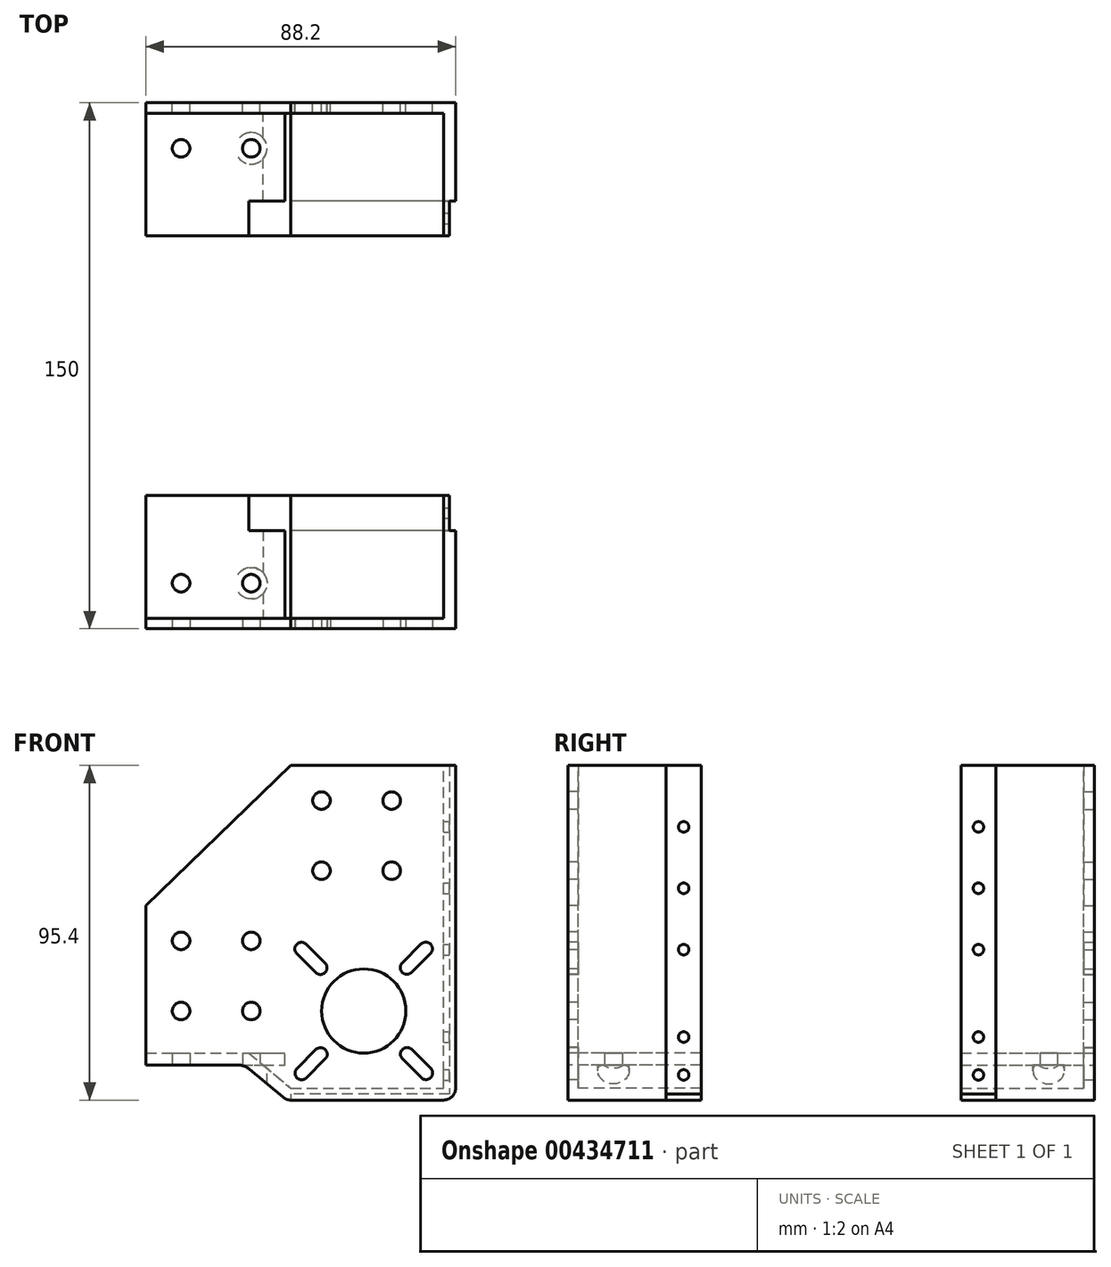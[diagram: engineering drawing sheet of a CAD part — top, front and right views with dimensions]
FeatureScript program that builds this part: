
annotation { "Feature Type Name" : "Feature", "Feature Type Description" : "" }
export const myFeature = defineFeature(function(context is Context, id is Id, definition is map)
    precondition{}
    {
        {
            assignVariable(context, id + "F0", {"name" : "Thickness", "anyValue" : 3});
        }
        {
            var Q0;
            Q0=qCreatedBy(makeId("Front.planeOp"),FACE);
            cPlane(context, id + "F1", {"entities" : qUnion([Q0]), "cplaneType" : CPlaneType.OFFSET, "offset" : 75 * mm, "width" : 150 * mm, "height" : 150 * mm});
        }
        {
            var Q0;
            Q0=qCreatedBy(id+"F1.planeOp",FACE);
            var sketch = newSketch(context, id + "F2", { "sketchPlane" : qUnion([Q0])});
            skLineSegment(sketch, "E0.bottom", {"start": v(-20, 20) * mm, "end": v(20, 20) * mm, "construction": true});
            skLineSegment(sketch, "E0.top", {"start": v(-20, -20) * mm, "end": v(20, -20) * mm, "construction": true});
            skLineSegment(sketch, "E0.left", {"start": v(-20, 20) * mm, "end": v(-20, -20) * mm, "construction": true});
            skLineSegment(sketch, "E0.right", {"start": v(20, 20) * mm, "end": v(20, -20) * mm, "construction": true});
            skLineSegment(sketch, "E1", {"start": v(0, 77.82) * mm, "end": v(0, -77.82) * mm, "construction": true});
            skLineSegment(sketch, "E2", {"start": v(-61.46, 0) * mm, "end": v(61.46, 0) * mm, "construction": true});
            skLineSegment(sketch, "E3", {"start": v(20, 20) * mm, "end": v(-20, -20) * mm, "construction": true});
            skLineSegment(sketch, "E4", {"start": v(-20, 20) * mm, "end": v(20, -20) * mm, "construction": true});
            skPoint(sketch, "E5", {"position": v(-15, 15) * mm});
            skPoint(sketch, "E6", {"position": v(-15, -15) * mm});
            skPoint(sketch, "E7", {"position": v(15, 15) * mm});
            skPoint(sketch, "E8", {"position": v(15, -15) * mm});
            skCircle(sketch, "E9", {"center": v(-15, 15) * mm, "radius": 1.9 * mm, "construction": true});
            skLineSegment(sketch, "E10", {"start": v(-17.69, 17.69) * mm, "end": v(-21.46, 13.92) * mm, "construction": true});
            skLineSegment(sketch, "E11", {"start": v(-17.69, 17.69) * mm, "end": v(-15.39, 19.99) * mm, "construction": true});
            skLineSegment(sketch, "E12", {"start": v(-12.31, 12.31) * mm, "end": v(-14.6, 10.03) * mm, "construction": true});
            skLineSegment(sketch, "E13", {"start": v(-12.31, 12.31) * mm, "end": v(-10.18, 14.45) * mm, "construction": true});
            skLineSegment(sketch, "E14", {"start": v(-19.03, 16.34) * mm, "end": v(-13.66, 10.97) * mm});
            skLineSegment(sketch, "E15", {"start": v(-16.34, 19.03) * mm, "end": v(-10.97, 13.66) * mm});
            skArc(sketch, "E16", {"start": v(-16.34, 19.03) * mm, "mid": v(-19.03, 19.03) * mm, "end": v(-19.03, 16.34) * mm});
            skArc(sketch, "E17", {"start": v(-19.03, 16.34) * mm, "mid": v(-16.34, 16.34) * mm, "end": v(-16.34, 19.03) * mm, "construction": true});
            skArc(sketch, "E18", {"start": v(-10.97, 13.66) * mm, "mid": v(-13.66, 13.66) * mm, "end": v(-13.66, 10.97) * mm, "construction": true});
            skArc(sketch, "E19", {"start": v(-13.66, 10.97) * mm, "mid": v(-10.97, 10.97) * mm, "end": v(-10.97, 13.66) * mm});
            skArc(sketch, "E20.1.0", {"start": v(-10.91, -13.7) * mm, "mid": v(-10.91, -11) * mm, "end": v(-13.6, -11) * mm});
            skLineSegment(sketch, "E20.1.1", {"start": v(-16.29, -19.07) * mm, "end": v(-10.91, -13.7) * mm});
            skArc(sketch, "E20.1.2", {"start": v(-18.98, -16.38) * mm, "mid": v(-18.98, -19.07) * mm, "end": v(-16.29, -19.07) * mm});
            skLineSegment(sketch, "E20.1.3", {"start": v(-18.98, -16.38) * mm, "end": v(-13.6, -11) * mm});
            skArc(sketch, "E20.2.0", {"start": v(13.75, -10.95) * mm, "mid": v(11.06, -10.95) * mm, "end": v(11.06, -13.64) * mm});
            skLineSegment(sketch, "E20.2.1", {"start": v(19.12, -16.33) * mm, "end": v(13.75, -10.95) * mm});
            skArc(sketch, "E20.2.2", {"start": v(16.44, -19.01) * mm, "mid": v(19.12, -19.01) * mm, "end": v(19.12, -16.33) * mm});
            skLineSegment(sketch, "E20.2.3", {"start": v(16.44, -19.01) * mm, "end": v(11.06, -13.64) * mm});
            skArc(sketch, "E20.3.0", {"start": v(11, 13.71) * mm, "mid": v(11, 11.02) * mm, "end": v(13.7, 11.02) * mm});
            skLineSegment(sketch, "E20.3.1", {"start": v(16.38, 19.09) * mm, "end": v(11, 13.71) * mm});
            skArc(sketch, "E20.3.2", {"start": v(19.07, 16.4) * mm, "mid": v(19.07, 19.09) * mm, "end": v(16.38, 19.09) * mm});
            skLineSegment(sketch, "E20.3.3", {"start": v(19.07, 16.4) * mm, "end": v(13.7, 11.02) * mm});
            skPoint(sketch, "E20.center", {"position": v(0.05, 0) * mm});
            skCircle(sketch, "E21", {"center": v(0.05, 0) * mm, "radius": 12 * mm});
            skSolve(sketch);
        }
        {
            var Q0;
            Q0=qCreatedBy(id+"F1.planeOp",FACE);
            var sketch = newSketch(context, id + "F3", { "sketchPlane" : qUnion([Q0])});
            skCircle(sketch, "E22.0", {"center": v(0.05, 0) * mm, "radius": 12 * mm});
            skArc(sketch, "E22.1", {"start": v(-13.66, 10.97) * mm, "mid": v(-10.97, 10.97) * mm, "end": v(-10.97, 13.66) * mm});
            skLineSegment(sketch, "E22.2", {"start": v(-16.34, 19.03) * mm, "end": v(-10.97, 13.66) * mm});
            skArc(sketch, "E22.3", {"start": v(-16.34, 19.03) * mm, "mid": v(-19.03, 19.03) * mm, "end": v(-19.03, 16.34) * mm});
            skLineSegment(sketch, "E22.4", {"start": v(-19.03, 16.34) * mm, "end": v(-13.66, 10.97) * mm});
            skLineSegment(sketch, "E22.5", {"start": v(16.38, 19.09) * mm, "end": v(11, 13.71) * mm});
            skArc(sketch, "E22.6", {"start": v(19.07, 16.4) * mm, "mid": v(19.07, 19.09) * mm, "end": v(16.38, 19.09) * mm});
            skLineSegment(sketch, "E22.7", {"start": v(19.07, 16.4) * mm, "end": v(13.7, 11.02) * mm});
            skArc(sketch, "E22.8", {"start": v(11, 13.71) * mm, "mid": v(11, 11.02) * mm, "end": v(13.7, 11.02) * mm});
            skLineSegment(sketch, "E22.9", {"start": v(19.12, -16.33) * mm, "end": v(13.75, -10.95) * mm});
            skArc(sketch, "E22.10", {"start": v(13.75, -10.95) * mm, "mid": v(11.06, -10.95) * mm, "end": v(11.06, -13.64) * mm});
            skLineSegment(sketch, "E22.11", {"start": v(16.44, -19.01) * mm, "end": v(11.06, -13.64) * mm});
            skArc(sketch, "E22.12", {"start": v(16.44, -19.01) * mm, "mid": v(19.12, -19.01) * mm, "end": v(19.12, -16.33) * mm});
            skLineSegment(sketch, "E22.13", {"start": v(-16.29, -19.07) * mm, "end": v(-10.91, -13.7) * mm});
            skArc(sketch, "E22.14", {"start": v(-10.91, -13.7) * mm, "mid": v(-10.91, -11) * mm, "end": v(-13.6, -11) * mm});
            skLineSegment(sketch, "E22.15", {"start": v(-18.98, -16.38) * mm, "end": v(-13.6, -11) * mm});
            skArc(sketch, "E22.16", {"start": v(-18.98, -16.38) * mm, "mid": v(-18.98, -19.07) * mm, "end": v(-16.29, -19.07) * mm});
            skLineSegment(sketch, "E22.17", {"start": v(-61.46, 0) * mm, "end": v(61.46, 0) * mm, "construction": true});
            skLineSegment(sketch, "E22.18", {"start": v(0, 77.82) * mm, "end": v(0, -77.82) * mm, "construction": true});
            skLineSegment(sketch, "E22.19", {"start": v(20, 20) * mm, "end": v(20, -20) * mm, "construction": true});
            skLineSegment(sketch, "E22.20", {"start": v(-20, 20) * mm, "end": v(20, 20) * mm, "construction": true});
            skLineSegment(sketch, "E22.21", {"start": v(-20, 20) * mm, "end": v(-20, -20) * mm, "construction": true});
            skLineSegment(sketch, "E22.22", {"start": v(-20, -20) * mm, "end": v(20, -20) * mm, "construction": true});
            skLineSegment(sketch, "E23.3", {"start": v(22.8, 22) * mm, "end": v(22.8, -22) * mm});
            skPoint(sketch, "E24", {"position": v(-32, -10) * mm});
            skPoint(sketch, "E25", {"position": v(-62, -10) * mm});
            skPoint(sketch, "E26", {"position": v(-32, 30) * mm});
            skLineSegment(sketch, "E27", {"start": v(-62, -10) * mm, "end": v(-62, 30) * mm});
            skLineSegment(sketch, "E28", {"start": v(-62, 30) * mm, "end": v(-32, 30) * mm});
            skLineSegment(sketch, "E29", {"start": v(-62, -10) * mm, "end": v(-32, -10) * mm, "construction": true});
            skLineSegment(sketch, "E30", {"start": v(-66.45, 10) * mm, "end": v(-57.93, 10) * mm, "construction": true});
            skPoint(sketch, "E30.startSnap0", {"position": v(-62, 10) * mm});
            skLineSegment(sketch, "E31", {"start": v(-57.93, 10) * mm, "end": v(-57.93, 30) * mm, "construction": true});
            skLineSegment(sketch, "E32", {"start": v(-62, 20) * mm, "end": v(-22, 20) * mm, "construction": true});
            skPoint(sketch, "E32.startSnap0", {"position": v(-57.93, 20) * mm});
            skLineSegment(sketch, "E33", {"start": v(-42, 20) * mm, "end": v(-42, 30) * mm, "construction": true});
            skLineSegment(sketch, "E34", {"start": v(-42, 31.86) * mm, "end": v(-62, 31.86) * mm, "construction": true});
            skLineSegment(sketch, "E35", {"start": v(-52, 31.86) * mm, "end": v(-52, 20) * mm, "construction": true});
            skCircle(sketch, "E36", {"center": v(-52, 20) * mm, "radius": 2.5 * mm});
            skCircle(sketch, "E37.MirrorC", {"center": v(-32, 20) * mm, "radius": 2.5 * mm});
            skCircle(sketch, "E38.MirrorC", {"center": v(-52, 0) * mm, "radius": 2.5 * mm});
            skCircle(sketch, "E39.MirrorC", {"center": v(-32, 0) * mm, "radius": 2.5 * mm});
            skLineSegment(sketch, "E40", {"start": v(-20, -20) * mm, "end": v(-32, -10) * mm, "construction": true});
            skLineSegment(sketch, "E41.1", {"start": v(-62, -12) * mm, "end": v(-32.72, -12) * mm});
            skLineSegment(sketch, "E42", {"start": v(22.8, -22) * mm, "end": v(-26.58, -22) * mm, "construction": true});
            skLineSegment(sketch, "E43", {"start": v(22.8, 22) * mm, "end": v(-20.72, 22) * mm, "construction": true});
            skLineSegment(sketch, "E44", {"start": v(-32, 30) * mm, "end": v(-20.72, 22) * mm, "construction": true});
            skLineSegment(sketch, "E45", {"start": v(-32.72, -12) * mm, "end": v(-20.72, -22) * mm});
            skLineSegment(sketch, "E46", {"start": v(-62, -12) * mm, "end": v(-62, -10) * mm});
            skLineSegment(sketch, "E47", {"start": v(-20.72, -22) * mm, "end": v(22.8, -22) * mm});
            skLineSegment(sketch, "E48", {"start": v(-20.72, 30) * mm, "end": v(-11.2, 22) * mm});
            skLineSegment(sketch, "E49", {"start": v(-20.72, 30) * mm, "end": v(-32, 30) * mm});
            skLineSegment(sketch, "E50", {"start": v(22.8, 22) * mm, "end": v(-11.2, 22) * mm});
            skLineSegment(sketch, "E51", {"start": v(-32, 36.5) * mm, "end": v(-32, 62.36) * mm, "construction": true});
            skLineSegment(sketch, "E52", {"start": v(-52, 36.5) * mm, "end": v(-52, 62.36) * mm, "construction": true});
            skLineSegment(sketch, "E53", {"start": v(-70.46, 40) * mm, "end": v(42.49, 40) * mm, "construction": true});
            skLineSegment(sketch, "E54", {"start": v(-73.98, 60) * mm, "end": v(42.49, 60) * mm, "construction": true});
            skLineSegment(sketch, "E55", {"start": v(22.8, 22) * mm, "end": v(22.8, 70) * mm});
            skLineSegment(sketch, "E56", {"start": v(22.8, 70) * mm, "end": v(-20.72, 70) * mm});
            skLineSegment(sketch, "E57", {"start": v(-20.72, 70) * mm, "end": v(-62, 30) * mm});
            skLineSegment(sketch, "E58", {"start": v(19.8, 70) * mm, "end": v(19.8, 24.67) * mm, "construction": true});
            skCircle(sketch, "E59", {"center": v(-12, 40) * mm, "radius": 2.5 * mm});
            skCircle(sketch, "E60", {"center": v(-12, 60) * mm, "radius": 2.5 * mm});
            skCircle(sketch, "E61", {"center": v(8, 60) * mm, "radius": 2.5 * mm});
            skCircle(sketch, "E62", {"center": v(8, 40) * mm, "radius": 2.5 * mm});
            skSolve(sketch);
        }
        {
            var Q0;
            Q0=qCreatedBy(id+"F1.planeOp",FACE);
            var sketch = newSketch(context, id + "F4", { "sketchPlane" : qUnion([Q0])});
            skLineSegment(sketch, "E63.0", {"start": v(-62, -12) * mm, "end": v(-32.72, -12) * mm});
            skLineSegment(sketch, "E63.1", {"start": v(-32.72, -12) * mm, "end": v(-20.72, -22) * mm});
            skLineSegment(sketch, "E63.2", {"start": v(-20.72, -22) * mm, "end": v(22.8, -22) * mm});
            skLineSegment(sketch, "E64.0", {"start": v(-21.96, -25.4) * mm, "end": v(22.8, -25.4) * mm});
            skLineSegment(sketch, "E64.1", {"start": v(-33.96, -15.4) * mm, "end": v(-21.96, -25.4) * mm});
            skLineSegment(sketch, "E64.2", {"start": v(-62, -15.4) * mm, "end": v(-33.96, -15.4) * mm});
            skLineSegment(sketch, "E65", {"start": v(-62, -15.4) * mm, "end": v(-62, -12) * mm});
            skLineSegment(sketch, "E66", {"start": v(22.8, -25.4) * mm, "end": v(22.8, -22) * mm});
            skLineSegment(sketch, "E67", {"start": v(-32.72, -12) * mm, "end": v(-22.4, -12) * mm});
            skLineSegment(sketch, "E68", {"start": v(-28.64, -15.4) * mm, "end": v(-22.4, -15.4) * mm});
            skLineSegment(sketch, "E69", {"start": v(-22.4, -15.4) * mm, "end": v(-22.4, -12) * mm});
            skPoint(sketch, "E70.1", {"position": v(-62, -10) * mm});
            skPoint(sketch, "E70.2", {"position": v(-62, 30) * mm});
            skLineSegment(sketch, "E71", {"start": v(-62, 30) * mm, "end": v(-62, -10) * mm, "construction": true});
            skLineSegment(sketch, "E72", {"start": v(-65.4, 30) * mm, "end": v(-65.4, -15.4) * mm, "construction": true});
            skLineSegment(sketch, "E73", {"start": v(-65.4, -15.4) * mm, "end": v(-62, -15.4) * mm, "construction": true});
            skLineSegment(sketch, "E74", {"start": v(-65.4, 30) * mm, "end": v(-62, 30) * mm, "construction": true});
            skLineSegment(sketch, "E75", {"start": v(-62, 30) * mm, "end": v(-62, -12) * mm, "construction": true});
            skPoint(sketch, "E76.0", {"position": v(22.8, 22) * mm});
            skLineSegment(sketch, "E77", {"start": v(26.2, 22) * mm, "end": v(26.2, -25.4) * mm});
            skLineSegment(sketch, "E78", {"start": v(26.2, -25.4) * mm, "end": v(22.8, -25.4) * mm});
            skLineSegment(sketch, "E79", {"start": v(26.2, 22) * mm, "end": v(22.8, 22) * mm, "construction": true});
            skLineSegment(sketch, "E80", {"start": v(22.8, 22) * mm, "end": v(22.8, -22) * mm});
            skPoint(sketch, "E81.0", {"position": v(22.8, 70) * mm});
            skLineSegment(sketch, "E82", {"start": v(22.8, 22) * mm, "end": v(22.8, 70) * mm});
            skLineSegment(sketch, "E83", {"start": v(26.2, 22) * mm, "end": v(26.2, 70) * mm});
            skLineSegment(sketch, "E84", {"start": v(26.2, 70) * mm, "end": v(22.8, 70) * mm});
            skSolve(sketch);
        }
        {
            var Q0;
            Q0=qSketchRegion(id+"F3",true);
            extrude(context, id + "F5", {"entities" : qUnion([Q0]), "oppositeDirection" : true, "depth" : (getVariable(context, 'Thickness')) * mm});
        }
        {
            var Q0;
            Q0=qSketchRegion(id+"F4",true);
            extrude(context, id + "F6", {"entities" : qUnion([Q0]), "operationType" : NewBodyOperationType.ADD, "oppositeDirection" : true, "depth" : 28 * mm});
        }
        {
            var Q0;
            Q0=makeQuery(id+"F6.opExtrude","SWEPT_FACE",FACE,{"disambiguationData":[OSD([sQuery(id+"F4.wireOp",EDGE,"E64.2")])]});
            var sketch = newSketch(context, id + "F7", { "sketchPlane" : qUnion([Q0])});
            skPoint(sketch, "E85.0", {"position": v(-62, 72) * mm});
            skPoint(sketch, "E86", {"position": v(-52, 62) * mm});
            skPoint(sketch, "E87", {"position": v(-32, 62) * mm});
            skCircle(sketch, "E88", {"center": v(-52, 62) * mm, "radius": 2.5 * mm});
            skCircle(sketch, "E89", {"center": v(-32, 62) * mm, "radius": 2.5 * mm});
            skCircle(sketch, "E90", {"center": v(-32, 62) * mm, "radius": 4.5 * mm});
            skSolve(sketch);
        }
        {
            var Q0;
            Q0=makeQuery(id+"F7.imprint","IMPRINT",FACE,{"disambiguationData":[TD([[makeQuery(id+"F7.imprint","IMPRINT",EDGE,{"derivedFrom":sQuery(id+"F7.wireOp",EDGE,"E89")}),1.0]])]});
            var Q1;
            Q1=makeQuery(id+"F7.imprint","IMPRINT",FACE,{"disambiguationData":[TD([[makeQuery(id+"F7.imprint","IMPRINT",EDGE,{"derivedFrom":sQuery(id+"F7.wireOp",EDGE,"E88")}),1.0]])]});
            var Q2;
            Q2=sQuery(id+"F7.wireOp",EDGE,"E88");
            var Q3;
            Q3=sQuery(id+"F7.wireOp",EDGE,"E89");
            extrude(context, id + "F8", {"entities" : qUnion([Q0, Q1]), "operationType" : NewBodyOperationType.REMOVE, "surfaceEntities" : qUnion([Q2, Q3]), "oppositeDirection" : true, "depth" : 25 * mm, "symmetric" : true});
        }
        {
            var Q0;
            {var subQ0=sQuery(id+"F7.wireOp",EDGE,"E89");var subQ1=makeQuery(id+"F6.opExtrude","SWEPT_EDGE",EDGE,{"disambiguationData":[OSD([sQuery(id+"F4.wireOp",EDGE,"E64.1"),sQuery(id+"F4.wireOp",EDGE,"E64.2")])]});var subQ2=makeQuery(id+"F7.imprint","INTERSECT",VERTEX,{"disambiguationData":[OD(0.0)],"derivedFrom":[subQ1,subQ0]});Q0=makeQuery(id+"F7.imprint","IMPRINT",FACE,{"disambiguationData":[TD([[makeQuery(id+"F7.imprint","IMPRINT",EDGE,{"disambiguationData":[TD([[subQ2,1.0]])],"derivedFrom":subQ0}),-1.0]])]});}
            var Q1;
            Q1=makeQuery(id+"F7.imprint","IMPRINT",FACE,{"disambiguationData":[TD([[makeQuery(id+"F7.imprint","IMPRINT",EDGE,{"derivedFrom":sQuery(id+"F7.wireOp",EDGE,"E89")}),-1.0]])]});
            var Q2;
            Q2=makeQuery(id+"F7.imprint","IMPRINT",FACE,{"disambiguationData":[TD([[makeQuery(id+"F7.imprint","IMPRINT",EDGE,{"derivedFrom":sQuery(id+"F7.wireOp",EDGE,"E89")}),1.0]])]});
            var Q3;
            Q3=makeQuery(id+"F6.opExtrude","SWEPT_FACE",FACE,{"disambiguationData":[OSD([sQuery(id+"F4.wireOp",EDGE,"E64.1")])]});
            extrude(context, id + "F9", {"entities" : qUnion([Q0, Q1, Q2]), "operationType" : NewBodyOperationType.REMOVE, "endBound" : BoundingType.UP_TO_SURFACE, "endBoundEntityFace" : qUnion([Q3]), "depth" : 25 * mm});
        }
        {
            var Q0;
            Q0=makeQuery(id+"F6.opExtrude","CAP_FACE",FACE,{"disambiguationData":[OSD([sQuery(id+"F4.wireOp",EDGE,"E63.0"),sQuery(id+"F4.wireOp",EDGE,"E63.1"),sQuery(id+"F4.wireOp",EDGE,"E63.2"),sQuery(id+"F4.wireOp",EDGE,"E64.0"),sQuery(id+"F4.wireOp",EDGE,"E64.1"),sQuery(id+"F4.wireOp",EDGE,"E64.2"),sQuery(id+"F4.wireOp",EDGE,"E65"),sQuery(id+"F4.wireOp",EDGE,"E67"),sQuery(id+"F4.wireOp",EDGE,"E68"),sQuery(id+"F4.wireOp",EDGE,"E69"),sQuery(id+"F4.wireOp",EDGE,"E77"),sQuery(id+"F4.wireOp",EDGE,"E78"),sQuery(id+"F4.wireOp",EDGE,"E80"),sQuery(id+"F4.wireOp",EDGE,"E82"),sQuery(id+"F4.wireOp",EDGE,"E83"),sQuery(id+"F4.wireOp",EDGE,"E84")])],"isStart":false});
            var sketch = newSketch(context, id + "F10", { "sketchPlane" : qUnion([Q0])});
            skLineSegment(sketch, "E91.0", {"start": v(-22.8, -22) * mm, "end": v(-22.8, 70) * mm});
            skLineSegment(sketch, "E92", {"start": v(-24.5, 70) * mm, "end": v(-24.5, -23.7) * mm});
            skLineSegment(sketch, "E93", {"start": v(-24.5, -25.4) * mm, "end": v(-22.8, -25.4) * mm, "construction": true});
            skLineSegment(sketch, "E94.0", {"start": v(33.96, -15.4) * mm, "end": v(21.96, -25.4) * mm});
            skLineSegment(sketch, "E94.1", {"start": v(62, -15.4) * mm, "end": v(33.96, -15.4) * mm});
            skLineSegment(sketch, "E94.2", {"start": v(32.72, -12) * mm, "end": v(20.72, -22) * mm});
            skLineSegment(sketch, "E94.3", {"start": v(20.72, -22) * mm, "end": v(-22.8, -22) * mm});
            skLineSegment(sketch, "E94.4", {"start": v(62, -12) * mm, "end": v(32.72, -12) * mm});
            skLineSegment(sketch, "E95", {"start": v(-22.8, 70) * mm, "end": v(-24.5, 70) * mm});
            skLineSegment(sketch, "E96", {"start": v(-22.8, -22) * mm, "end": v(-22.8, -23.7) * mm, "construction": true});
            skLineSegment(sketch, "E97", {"start": v(-24.5, -23.7) * mm, "end": v(20.72, -23.7) * mm});
            skPoint(sketch, "E97.startSnap0", {"position": v(-22.8, -23.7) * mm});
            skLineSegment(sketch, "E98", {"start": v(20.72, -23.7) * mm, "end": v(20.72, -25.4) * mm});
            skLineSegment(sketch, "E99", {"start": v(-24.5, -23.7) * mm, "end": v(-24.5, -25.4) * mm, "construction": true});
            skLineSegment(sketch, "E100", {"start": v(-22.8, -25.4) * mm, "end": v(21.96, -25.4) * mm, "construction": true});
            skLineSegment(sketch, "E101", {"start": v(-22.8, -23.7) * mm, "end": v(-22.8, -25.4) * mm, "construction": true});
            skSolve(sketch);
        }
        {
            var Q0;
            Q0=makeQuery(id+"F10.imprint","IMPRINT",FACE,{"disambiguationData":[TD([[makeQuery(id+"F10.imprint","IMPRINT",EDGE,{"derivedFrom":sQuery(id+"F10.wireOp",EDGE,"E91.0")}),1.0]])]});
            extrude(context, id + "F11", {"entities" : qUnion([Q0]), "operationType" : NewBodyOperationType.ADD, "depth" : 10 * mm});
        }
        {
            var Q0;
            Q0=makeQuery(id+"F11.opExtrude","SWEPT_FACE",FACE,{"disambiguationData":[OSD([sQuery(id+"F10.wireOp",EDGE,"E92")])]});
            var sketch = newSketch(context, id + "F12", { "sketchPlane" : qUnion([Q0])});
            skLineSegment(sketch, "E102", {"start": v(-42, 70) * mm, "end": v(-42, -23.7) * mm, "construction": true});
            skLineSegment(sketch, "E103", {"start": v(-2.4, 0) * mm, "end": v(-113.54, 0) * mm, "construction": true});
            skCircle(sketch, "E104", {"center": v(-42, -7.43) * mm, "radius": 1.5 * mm});
            skCircle(sketch, "E105", {"center": v(-42, -18.22) * mm, "radius": 1.5 * mm});
            skCircle(sketch, "E106", {"center": v(-42, 52.5) * mm, "radius": 1.5 * mm});
            skCircle(sketch, "E107", {"center": v(-42, 35) * mm, "radius": 1.5 * mm});
            skCircle(sketch, "E108", {"center": v(-42, 17.5) * mm, "radius": 1.5 * mm});
            skLineSegment(sketch, "E109", {"start": v(-29.87, 70) * mm, "end": v(-29.87, 0) * mm, "construction": true});
            skLineSegment(sketch, "E110", {"start": v(-29.87, 35) * mm, "end": v(-64.93, 35) * mm, "construction": true});
            skLineSegment(sketch, "E111", {"start": v(-27.67, 35) * mm, "end": v(-27.67, 0) * mm, "construction": true});
            skLineSegment(sketch, "E112", {"start": v(-27.67, 17.5) * mm, "end": v(-64.93, 17.5) * mm, "construction": true});
            skPoint(sketch, "E112.endSnap0", {"position": v(-27.67, 17.5) * mm});
            skLineSegment(sketch, "E113", {"start": v(-25.64, 35) * mm, "end": v(-25.64, 70) * mm, "construction": true});
            skLineSegment(sketch, "E114", {"start": v(-25.64, 52.5) * mm, "end": v(-64.93, 52.5) * mm, "construction": true});
            skSolve(sketch);
        }
        {
            var Q0;
            Q0=qSketchRegion(id+"F12",true);
            var Q1;
            Q1=makeQuery(id+"F11.boolean.opBoolean","MERGE",FACE,{"derivedFrom":[makeQuery(id+"F6.opExtrude","SWEPT_FACE",FACE,{"disambiguationData":[OSD([sQuery(id+"F4.wireOp",EDGE,"E80"),sQuery(id+"F4.wireOp",EDGE,"E82")])]}),makeQuery(id+"F11.opExtrude","SWEPT_FACE",FACE,{"disambiguationData":[OSD([sQuery(id+"F10.wireOp",EDGE,"E91.0")])]})]});
            extrude(context, id + "F13", {"entities" : qUnion([Q0]), "operationType" : NewBodyOperationType.REMOVE, "endBound" : BoundingType.UP_TO_SURFACE, "oppositeDirection" : true, "endBoundEntityFace" : qUnion([Q1]), "depth" : 25 * mm});
        }
        {
            var Q0;
            Q0=makeQuery(id+"F6.opExtrude","SWEPT_EDGE",EDGE,{"disambiguationData":[OSD([sQuery(id+"F4.wireOp",EDGE,"E72"),sQuery(id+"F4.wireOp",EDGE,"E74")])]});
            var Q1;
            Q1=makeQuery(id+"F6.opExtrude","SWEPT_EDGE",EDGE,{"disambiguationData":[OSD([sQuery(id+"F4.wireOp",EDGE,"E72"),sQuery(id+"F4.wireOp",EDGE,"E73")])]});
            var Q2;
            Q2=makeQuery(id+"F6.opExtrude","SWEPT_EDGE",EDGE,{"disambiguationData":[OSD([sQuery(id+"F4.wireOp",EDGE,"E64.0"),sQuery(id+"F4.wireOp",EDGE,"E64.1")])]});
            var Q3;
            Q3=makeQuery(id+"F6.opExtrude","SWEPT_EDGE",EDGE,{"disambiguationData":[OSD([sQuery(id+"F4.wireOp",EDGE,"E77"),sQuery(id+"F4.wireOp",EDGE,"E78")])]});
            var Q4;
            Q4=makeQuery(id+"F6.opExtrude","SWEPT_EDGE",EDGE,{"disambiguationData":[OSD([sQuery(id+"F4.wireOp",EDGE,"E77"),sQuery(id+"F4.wireOp",EDGE,"E79")])]});
            fillet(context, id + "F14", {"entities" : qUnion([Q0, Q1, Q2, Q3, Q4]), "radius" : (0.4 + getVariable(context, 'Thickness')) * mm, "tangentPropagation" : true, "allowEdgeOverflow" : false});
        }
        {
            var Q0;
            {var subQ0=sQuery(id+"F4.wireOp",EDGE,"E73");var subQ1=sQuery(id+"F4.wireOp",EDGE,"E64.2");var subQ2=sQuery(id+"F4.wireOp",EDGE,"E64.1");var subQ3=sQuery(id+"F4.wireOp",EDGE,"E68");Q0=makeQuery(id+"F9.boolean.opBoolean","SPLIT",EDGE,{"disambiguationData":[TD([makeQuery(id+"F6.opExtrude","CAP_FACE",FACE,{"disambiguationData":[OSD([sQuery(id+"F4.wireOp",EDGE,"E63.0"),sQuery(id+"F4.wireOp",EDGE,"E63.1"),sQuery(id+"F4.wireOp",EDGE,"E63.2"),sQuery(id+"F4.wireOp",EDGE,"E64.0"),subQ2,subQ1,sQuery(id+"F4.wireOp",EDGE,"E66"),sQuery(id+"F4.wireOp",EDGE,"E67"),subQ3,sQuery(id+"F4.wireOp",EDGE,"E69"),sQuery(id+"F4.wireOp",EDGE,"E72"),subQ0,sQuery(id+"F4.wireOp",EDGE,"E74"),sQuery(id+"F4.wireOp",EDGE,"E75")])],"isStart":true})])],"derivedFrom":makeQuery(id+"F6.opExtrude","SWEPT_EDGE",EDGE,{"disambiguationData":[OSD([subQ2,subQ1])]})});}
            var Q1;
            {var subQ0=sQuery(id+"F4.wireOp",EDGE,"E68");var subQ1=sQuery(id+"F4.wireOp",EDGE,"E73");var subQ2=sQuery(id+"F4.wireOp",EDGE,"E64.2");var subQ3=sQuery(id+"F4.wireOp",EDGE,"E64.1");Q1=makeQuery(id+"F9.boolean.opBoolean","SPLIT",EDGE,{"disambiguationData":[TD([makeQuery(id+"F6.opExtrude","CAP_FACE",FACE,{"disambiguationData":[OSD([sQuery(id+"F4.wireOp",EDGE,"E63.0"),sQuery(id+"F4.wireOp",EDGE,"E63.1"),sQuery(id+"F4.wireOp",EDGE,"E63.2"),sQuery(id+"F4.wireOp",EDGE,"E64.0"),subQ3,subQ2,sQuery(id+"F4.wireOp",EDGE,"E66"),sQuery(id+"F4.wireOp",EDGE,"E67"),subQ0,sQuery(id+"F4.wireOp",EDGE,"E69"),sQuery(id+"F4.wireOp",EDGE,"E72"),subQ1,sQuery(id+"F4.wireOp",EDGE,"E74"),sQuery(id+"F4.wireOp",EDGE,"E75")])],"isStart":false})])],"derivedFrom":makeQuery(id+"F6.opExtrude","SWEPT_EDGE",EDGE,{"disambiguationData":[OSD([subQ3,subQ2])]})});}
            fillet(context, id + "F15", {"entities" : qUnion([Q0, Q1]), "radius" : 5 * mm, "tangentPropagation" : true, "allowEdgeOverflow" : false});
        }
        {
            var Q0;
            Q0=makeQuery(id+"F5.opExtrude","SWEPT_BODY",BODY,{"disambiguationData":[OSD([sQuery(id+"F3.wireOp",EDGE,"E22.0"),sQuery(id+"F3.wireOp",EDGE,"E22.1"),sQuery(id+"F3.wireOp",EDGE,"E22.2"),sQuery(id+"F3.wireOp",EDGE,"E22.3"),sQuery(id+"F3.wireOp",EDGE,"E22.4"),sQuery(id+"F3.wireOp",EDGE,"E22.5"),sQuery(id+"F3.wireOp",EDGE,"E22.6"),sQuery(id+"F3.wireOp",EDGE,"E22.7"),sQuery(id+"F3.wireOp",EDGE,"E22.8"),sQuery(id+"F3.wireOp",EDGE,"E22.9"),sQuery(id+"F3.wireOp",EDGE,"E22.10"),sQuery(id+"F3.wireOp",EDGE,"E22.11"),sQuery(id+"F3.wireOp",EDGE,"E22.12"),sQuery(id+"F3.wireOp",EDGE,"E22.13"),sQuery(id+"F3.wireOp",EDGE,"E22.14"),sQuery(id+"F3.wireOp",EDGE,"E22.15"),sQuery(id+"F3.wireOp",EDGE,"E22.16"),sQuery(id+"F3.wireOp",EDGE,"E23.3"),sQuery(id+"F3.wireOp",EDGE,"E27"),sQuery(id+"F3.wireOp",EDGE,"E28"),sQuery(id+"F3.wireOp",EDGE,"E36"),sQuery(id+"F3.wireOp",EDGE,"E37.MirrorC"),sQuery(id+"F3.wireOp",EDGE,"E38.MirrorC"),sQuery(id+"F3.wireOp",EDGE,"E39.MirrorC"),sQuery(id+"F3.wireOp",EDGE,"E41.1"),sQuery(id+"F3.wireOp",EDGE,"E45"),sQuery(id+"F3.wireOp",EDGE,"E46"),sQuery(id+"F3.wireOp",EDGE,"E47"),sQuery(id+"F3.wireOp",EDGE,"E48"),sQuery(id+"F3.wireOp",EDGE,"E49"),sQuery(id+"F3.wireOp",EDGE,"E50")])]});
            var Q1;
            Q1=qCreatedBy(makeId("Front.planeOp"),FACE);
            mirror(context, id + "F16", {"entities" : qUnion([Q0]), "mirrorPlane" : qUnion([Q1])});
        }
    });
